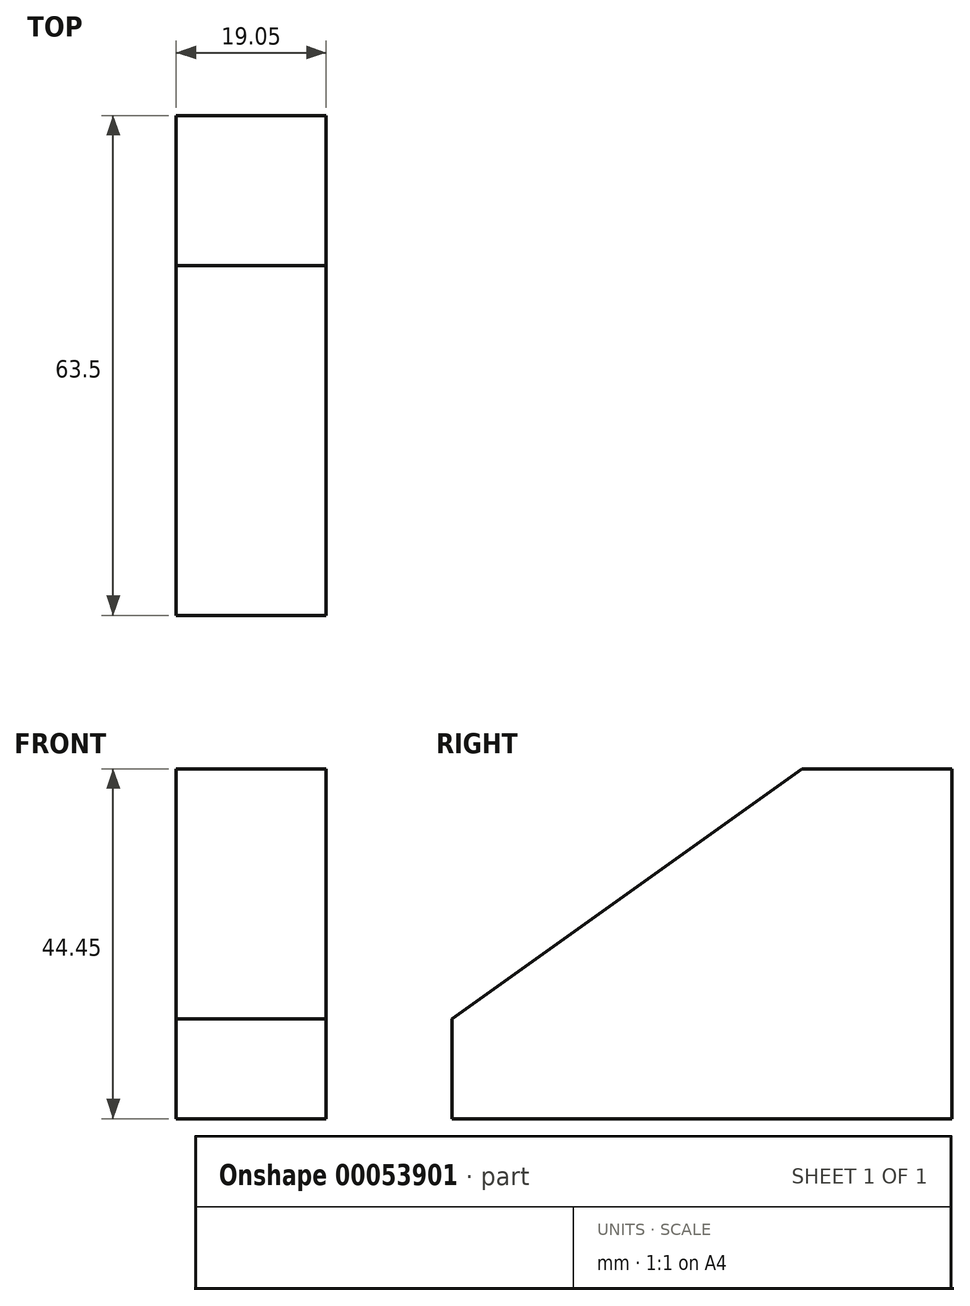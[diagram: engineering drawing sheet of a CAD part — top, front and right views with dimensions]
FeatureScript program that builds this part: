
annotation { "Feature Type Name" : "Feature", "Feature Type Description" : "" }
export const myFeature = defineFeature(function(context is Context, id is Id, definition is map)
    precondition{}
    {
        {
            var Q0;
            Q0=qCreatedBy(makeId("Right.planeOp"),FACE);
            var sketch = newSketch(context, id + "F0", { "sketchPlane" : qUnion([Q0])});
            skLineSegment(sketch, "E0", {"start": v(17.3, 30.92) * mm, "end": v(36.35, 30.92) * mm});
            skLineSegment(sketch, "E1", {"start": v(36.35, 30.92) * mm, "end": v(36.35, -13.53) * mm});
            skLineSegment(sketch, "E2", {"start": v(36.35, -13.53) * mm, "end": v(-27.15, -13.53) * mm});
            skLineSegment(sketch, "E3", {"start": v(-27.15, -13.53) * mm, "end": v(-27.15, -0.83) * mm});
            skLineSegment(sketch, "E4", {"start": v(-27.15, -0.83) * mm, "end": v(17.3, 30.92) * mm});
            skSolve(sketch);
        }
        {
            var Q0;
            Q0=makeQuery(id+"F0.imprint","IMPRINT",FACE,{"disambiguationData":[TD([[makeQuery(id+"F0.imprint","IMPRINT",EDGE,{"derivedFrom":sQuery(id+"F0.wireOp",EDGE,"E0")}),-1.0]])]});
            extrude(context, id + "F1", {"entities" : qUnion([Q0]), "depth" : 19.05 * mm});
        }
    });
